# Revit family: assa_abloy_cleanroom_04
name_source: partatom
category: Doors
units: mm (PartAtom-declared; Revit-internal decimal feet)

## family parameters
Always vertical = Yes
Classification Number = 23.30.10.00
Cut with Voids When Loaded = No
Host = Wall
Room Calculation Point = No
Shared = No

## types (4) — shared parameters
Analytic Construction = <None>
BIMobject category = Sliding Doors
Bottom Profile Height = Fixed Panel : 0'  4"
Bottom Profile Option 01 = Fixed Panel : 0'  4"
Bottom Profile Option 02 = Fixed Panel : 0'  7"
Bottom Profile Option 03 = Fixed Panel : 0'  10"
Bottom Profile Option 04 = Fixed Panel : 0'  12"
Brass Polished Finish = Brass, Polished
Brass Satin Finish = Brass, Satin
Clear Anodized = Clear Anodized
Dark Bronze Anodized = Dark Bronze Anodized
Date of publishing = 2015-02-23
Depth = 0.00
Disclaimer = Consult product specification for sensors to comply with ANSI A156.10.
Edition number = 1
Frame Material = Clear Anodized
Function = Interior
Gap = 0' - 0 1/4"
Glass = Glass
Height = 7' - 5 3/4"
IFC Classification = Door
Leaf Height = 6' - 9 1/8"
Manufacturer name = Besam-North America
Material main = Aluminium
NBS Reference Code = 25-30-20-77
NBS Reference Description = Sliding Doorset Systems
Nominal height = 0.00
Nominal width = 0.00
Product SKU = SL500_Clnrm_OHC
Product data url = http://besam-na.bimobject.com
Product family = Sliding
Product group = Clean Room
QR code = http://besam-na.bimobject.com
Rough Height = 7' - 6"
Rubber = Rubber, Black
Stainless Steel Polished Finish = Stainless Steel, Polished
Stainless Steel Satin Finish = Stainless Steel, Satin
UNSPSC Code = 301715
Uniclass 1.4 Code = L4133
Uniclass 1.4 Description = Sliding
Uniclass 2.0 Code = SS-25-30-20-77
Uniclass 2.0 Description = Sliding Doorset Systems
Wall Closure = By host
Weight Net (Kg) = 0

## per-type parameters (varying)
| type | Leaf Width | Rough Width | Width |
| OHC-7' | 3' - 5 1/2" | 7' - 0 1/2" | 7' - 0" |
| OHC- 8' | 3' - 11 1/2" | 8' - 0 1/2" | 8' - 0" |
| OHC- 8' 6'' | 4' - 2 1/2" | 8' - 6 1/2" | 8' - 6" |
| OHC- 9' | 4' - 5 1/2" | 9' - 0 1/2" | 9' - 0" |

## geometry (parser evidence)
native form markers: Blend x6, Sweep x27
no freeform markers — native parametric forms only
